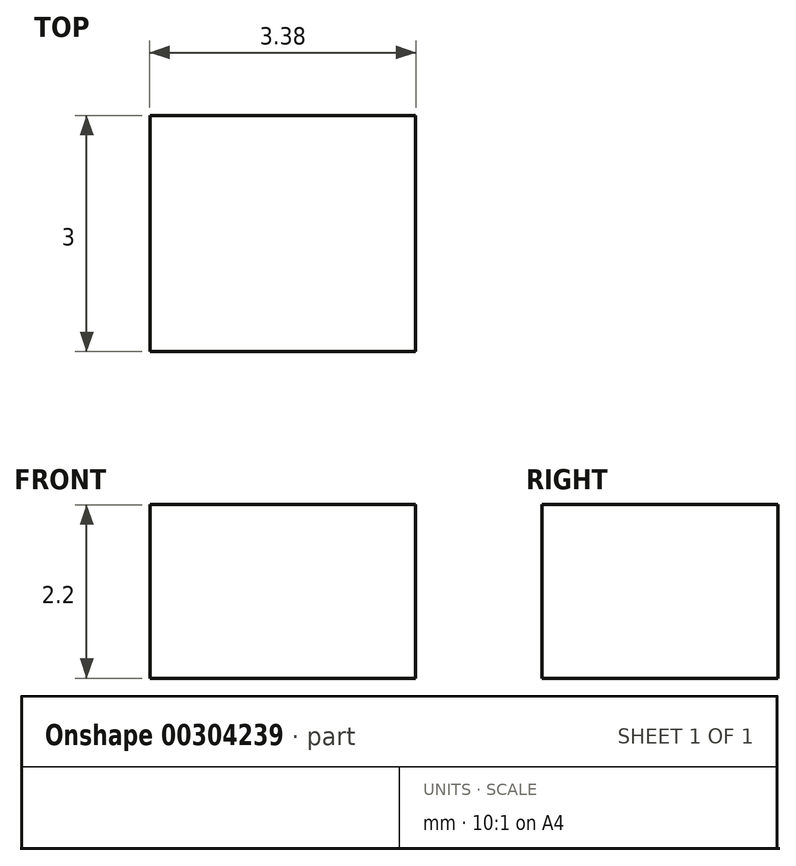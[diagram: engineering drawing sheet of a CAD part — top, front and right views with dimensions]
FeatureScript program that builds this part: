
annotation { "Feature Type Name" : "Feature", "Feature Type Description" : "" }
export const myFeature = defineFeature(function(context is Context, id is Id, definition is map)
    precondition{}
    {
        {
            var Q0;
            Q0=qCreatedBy(makeId("Front.planeOp"),FACE);
            var sketch = newSketch(context, id + "F0", { "sketchPlane" : qUnion([Q0])});
            skLineSegment(sketch, "E0.bottom", {"start": v(1.69, -1.1) * mm, "end": v(-1.69, -1.1) * mm});
            skLineSegment(sketch, "E0.top", {"start": v(1.69, 1.1) * mm, "end": v(-1.69, 1.1) * mm});
            skLineSegment(sketch, "E0.left", {"start": v(1.69, -1.1) * mm, "end": v(1.69, 1.1) * mm});
            skLineSegment(sketch, "E0.right", {"start": v(-1.69, -1.1) * mm, "end": v(-1.69, 1.1) * mm});
            skPoint(sketch, "E0.middle", {"position": v(0, 0) * mm});
            skSolve(sketch);
        }
        {
            var Q0;
            Q0=makeQuery(id+"F0.imprint","IMPRINT",FACE,{"disambiguationData":[TD([[makeQuery(id+"F0.imprint","IMPRINT",EDGE,{"derivedFrom":sQuery(id+"F0.wireOp",EDGE,"E0.bottom")}),-1.0]])]});
            extrude(context, id + "F1", {"entities" : qUnion([Q0]), "endBound" : BoundingType.SYMMETRIC, "depth" : 3 * mm});
        }
    });
